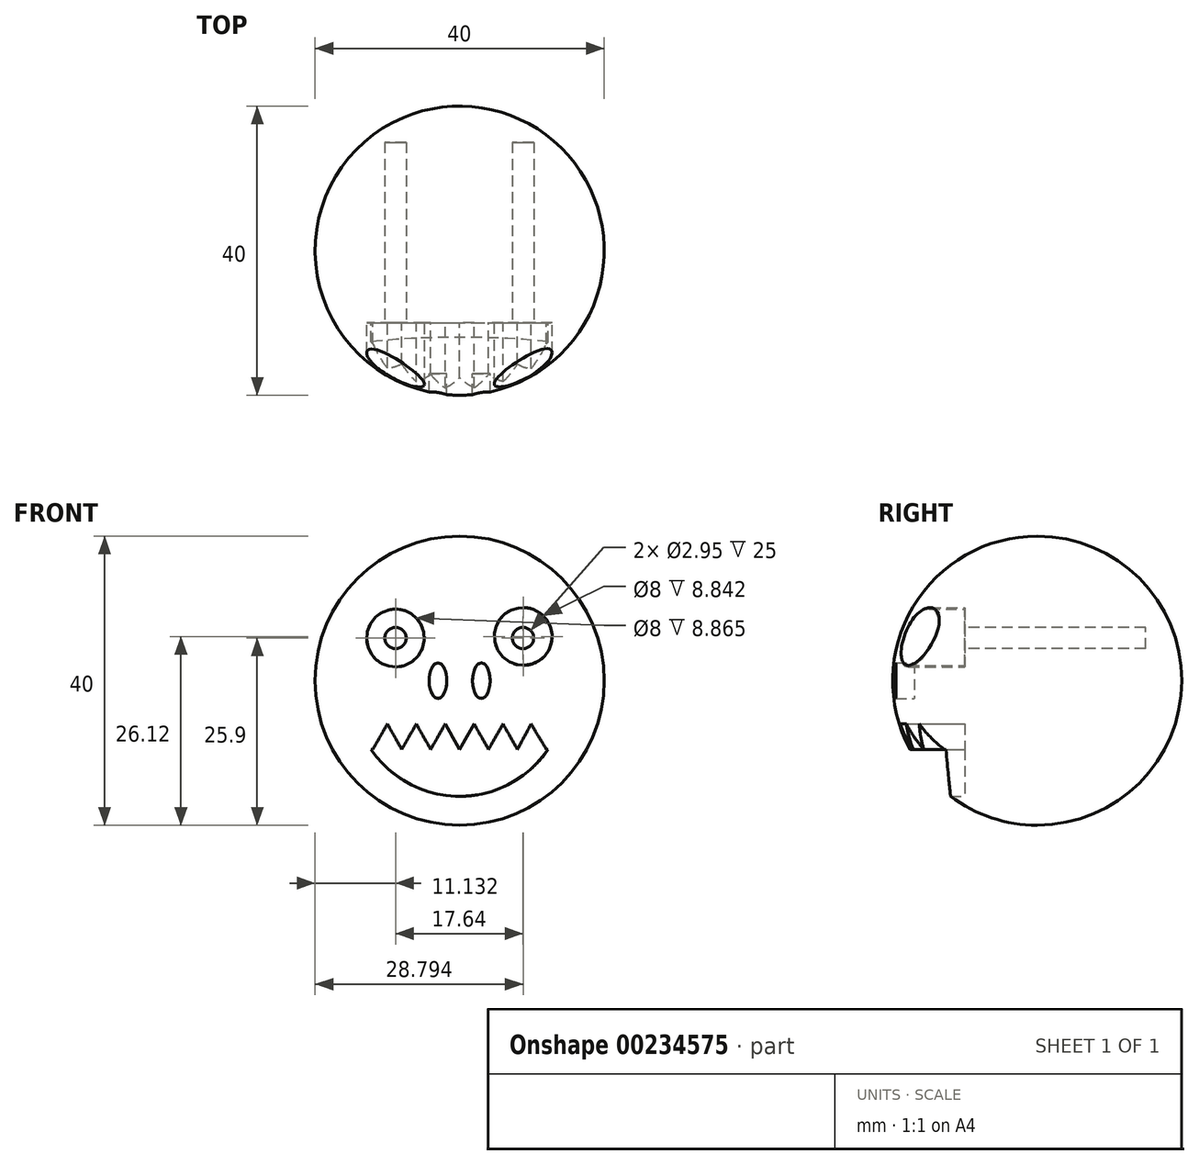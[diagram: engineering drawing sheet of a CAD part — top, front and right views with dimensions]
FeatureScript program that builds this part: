
annotation { "Feature Type Name" : "Feature", "Feature Type Description" : "" }
export const myFeature = defineFeature(function(context is Context, id is Id, definition is map)
    precondition{}
    {
        {
            var Q0;
            Q0=qCreatedBy(makeId("Front.planeOp"),FACE);
            var sketch = newSketch(context, id + "F0", { "sketchPlane" : qUnion([Q0])});
            skArc(sketch, "E0", {"start": v(0, 20) * mm, "mid": v(-20, 0) * mm, "end": v(0, -20) * mm});
            skLineSegment(sketch, "E1", {"start": v(0, 0) * mm, "end": v(0, 20) * mm});
            skLineSegment(sketch, "E2", {"start": v(0, 0) * mm, "end": v(0, -20) * mm});
            skSolve(sketch);
        }
        {
            var Q0;
            Q0=makeQuery(id+"F0.imprint","IMPRINT",FACE,{"disambiguationData":[TD([[makeQuery(id+"F0.imprint","IMPRINT",EDGE,{"derivedFrom":sQuery(id+"F0.wireOp",EDGE,"E0")}),1.0]])]});
            var Q1;
            Q1=sQuery(id+"F0.wireOp",EDGE,"E2");
            revolve(context, id + "F1", {"entities" : qUnion([Q0]), "axis" : qUnion([Q1]), "revolveType" : RevolveType.FULL});
        }
        {
            var Q0;
            Q0=qCreatedBy(makeId("Front.planeOp"),FACE);
            cPlane(context, id + "F2", {"entities" : qUnion([Q0]), "cplaneType" : CPlaneType.OFFSET, "offset" : 10 * mm, "width" : 150 * mm, "height" : 150 * mm});
        }
        {
            var Q0;
            Q0=qCreatedBy(id+"F2.planeOp",FACE);
            var sketch = newSketch(context, id + "F3", { "sketchPlane" : qUnion([Q0])});
            skLineSegment(sketch, "E3", {"start": v(0, 0) * mm, "end": v(0, 20.17) * mm});
            skLineSegment(sketch, "E4", {"start": v(0, 20.17) * mm, "end": v(0, -20.4) * mm});
            skPoint(sketch, "E5.endSnap0", {"position": v(0, -0.1) * mm});
            skPoint(sketch, "E6", {"position": v(-8.87, 5.9) * mm});
            skPoint(sketch, "E7", {"position": v(8.8, 6.12) * mm});
            skCircle(sketch, "E8", {"center": v(-8.87, 5.9) * mm, "radius": 4 * mm});
            skCircle(sketch, "E9", {"center": v(8.8, 6.12) * mm, "radius": 4 * mm});
            skSolve(sketch);
        }
        {
            var Q0;
            Q0 = qSketchRegion(id + "F3", true);
            var Q1;
            Q1=sQuery(id+"F3.wireOp",EDGE,"E8");
            var Q2;
            Q2=sQuery(id+"F3.wireOp",EDGE,"E9");
            extrude(context, id + "F4", {"entities" : qUnion([Q0]), "operationType" : NewBodyOperationType.REMOVE, "surfaceEntities" : qUnion([Q1, Q2]), "depth" : 10 * mm});
        }
        {
            var Q0;
            Q0=qCreatedBy(id+"F2.planeOp",FACE);
            cPlane(context, id + "F5", {"entities" : qUnion([Q0]), "cplaneType" : CPlaneType.OFFSET, "offset" : 7 * mm, "width" : 150 * mm, "height" : 150 * mm});
        }
        {
            var Q0;
            Q0=qCreatedBy(id+"F5.planeOp",FACE);
            var sketch = newSketch(context, id + "F6", { "sketchPlane" : qUnion([Q0])});
            skPoint(sketch, "E10", {"position": v(-3, 0) * mm});
            skEllipse(sketch, "E11", {"center": v(-3, 0) * mm, "majorRadius": 2.5 * mm, "minorRadius": 1.22 * mm, "majorAxis": v(0, 1)});
            skEllipse(sketch, "E12.MirrorC", {"center": v(3, 0) * mm, "majorRadius": 2.5 * mm, "minorRadius": 1.22 * mm, "majorAxis": v(0, 1)});
            skSolve(sketch);
        }
        {
            var Q0;
            Q0 = qSketchRegion(id + "F6", true);
            var Q1;
            Q1=sQuery(id+"F6.wireOp",EDGE,"E11");
            extrude(context, id + "F7", {"entities" : qUnion([Q0]), "operationType" : NewBodyOperationType.REMOVE, "surfaceEntities" : qUnion([Q1]), "depth" : 25 * mm});
        }
        {
            var Q0;
            Q0=qCreatedBy(id+"F2.planeOp",FACE);
            var sketch = newSketch(context, id + "F8", { "sketchPlane" : qUnion([Q0])});
            skLineSegment(sketch, "E13", {"start": v(0, 0) * mm, "end": v(0, -1.2) * mm});
            skArc(sketch, "E14", {"start": v(-14, -6) * mm, "mid": v(0, -16) * mm, "end": v(14, -6) * mm});
            skPoint(sketch, "E15.end.orphan", {"position": v(0, -16) * mm});
            skPoint(sketch, "E16.start.orphan", {"position": v(0, -6) * mm});
            skLineSegment(sketch, "E17", {"start": v(2, -6) * mm, "end": v(0, -9.5) * mm});
            skLineSegment(sketch, "E18", {"start": v(-2, -6) * mm, "end": v(0, -9.5) * mm});
            skLineSegment(sketch, "E19", {"start": v(9.9, -6) * mm, "end": v(10, -6) * mm});
            skLineSegment(sketch, "E20", {"start": v(12, -9.5) * mm, "end": v(12.25, -9.5) * mm});
            skLineSegment(sketch, "E21", {"start": v(12.25, -9.5) * mm, "end": v(12, -9.5) * mm});
            skLineSegment(sketch, "E22", {"start": v(-12, -9.5) * mm, "end": v(-10, -6) * mm});
            skLineSegment(sketch, "E23", {"start": v(-8, -9.5) * mm, "end": v(-10, -6) * mm});
            skLineSegment(sketch, "E24", {"start": v(-8, -9.5) * mm, "end": v(-6, -6) * mm});
            skLineSegment(sketch, "E25", {"start": v(-4, -9.5) * mm, "end": v(-6, -6) * mm});
            skLineSegment(sketch, "E26", {"start": v(-4, -9.5) * mm, "end": v(-2, -6) * mm});
            skLineSegment(sketch, "E27", {"start": v(2, -6) * mm, "end": v(4, -9.5) * mm});
            skLineSegment(sketch, "E28", {"start": v(6, -6) * mm, "end": v(4, -9.5) * mm});
            skLineSegment(sketch, "E29", {"start": v(6, -6) * mm, "end": v(8, -9.5) * mm});
            skLineSegment(sketch, "E30", {"start": v(8, -9.5) * mm, "end": v(9.9, -6) * mm});
            skLineSegment(sketch, "E31", {"start": v(9.9, -6) * mm, "end": v(12, -9.5) * mm});
            skPoint(sketch, "E32.start.orphan", {"position": v(12, -6) * mm});
            skPoint(sketch, "E33.start.orphan", {"position": v(8, -6) * mm});
            skPoint(sketch, "E34.start.orphan", {"position": v(4, -6) * mm});
            skPoint(sketch, "E35.start.orphan", {"position": v(-4, -6) * mm});
            skPoint(sketch, "E36.start.orphan", {"position": v(-8, -6) * mm});
            skPoint(sketch, "E37.start.orphan", {"position": v(-12, -6) * mm});
            skLineSegment(sketch, "E38.trimOffspring", {"start": v(-12, -9.5) * mm, "end": v(-12.25, -9.5) * mm});
            skLineSegment(sketch, "E39", {"start": v(10, -6) * mm, "end": v(9.9, -6) * mm});
            skSolve(sketch);
        }
        {
            var Q0;
            Q0 = qSketchRegion(id + "F8", true);
            extrude(context, id + "F9", {"entities" : qUnion([Q0]), "operationType" : NewBodyOperationType.REMOVE, "depth" : 25 * mm});
        }
        {
            var Q0;
            Q0=qCreatedBy(makeId("Front.planeOp"),FACE);
            var sketch = newSketch(context, id + "F10", { "sketchPlane" : qUnion([Q0])});
            skCircle(sketch, "E40", {"center": v(-8.87, 5.9) * mm, "radius": 1.48 * mm});
            skCircle(sketch, "E41", {"center": v(8.77, 5.9) * mm, "radius": 1.48 * mm});
            skSolve(sketch);
        }
        {
            var Q0;
            Q0 = qSketchRegion(id + "F10", true);
            extrude(context, id + "F11", {"entities" : qUnion([Q0]), "operationType" : NewBodyOperationType.REMOVE, "oppositeDirection" : true, "depth" : 15 * mm});
        }
        {
            var Q0;
            Q0 = qSketchRegion(id + "F10", true);
            extrude(context, id + "F12", {"entities" : qUnion([Q0]), "operationType" : NewBodyOperationType.REMOVE, "depth" : 25 * mm});
        }
    });
